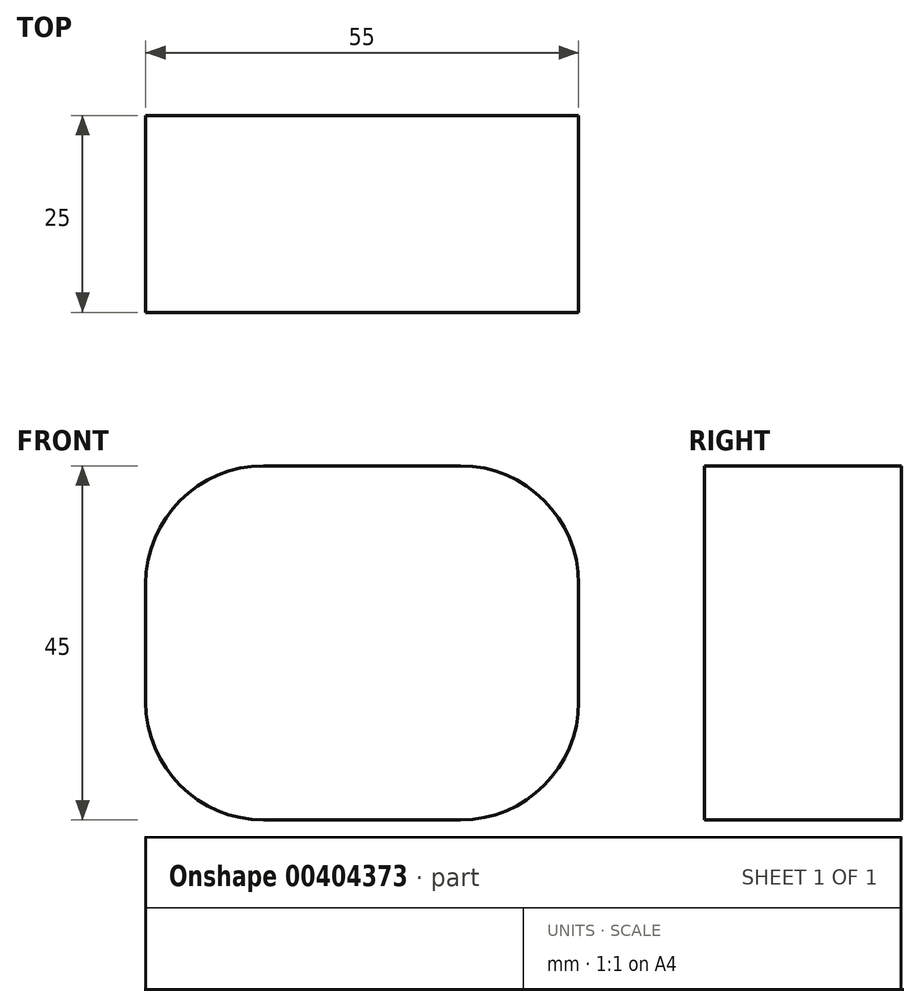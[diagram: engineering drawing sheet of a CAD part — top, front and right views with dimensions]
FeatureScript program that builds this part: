
annotation { "Feature Type Name" : "Feature", "Feature Type Description" : "" }
export const myFeature = defineFeature(function(context is Context, id is Id, definition is map)
    precondition{}
    {
        {
            var Q0;
            Q0=qCreatedBy(makeId("Front.planeOp"),FACE);
            var sketch = newSketch(context, id + "F0", { "sketchPlane" : qUnion([Q0])});
            skLineSegment(sketch, "E0.bottom", {"start": v(-12.5, 22.5) * mm, "end": v(12.5, 22.5) * mm});
            skLineSegment(sketch, "E0.top", {"start": v(-12.5, -22.5) * mm, "end": v(12.5, -22.5) * mm});
            skLineSegment(sketch, "E0.left", {"start": v(-27.5, 7.5) * mm, "end": v(-27.5, -7.5) * mm});
            skLineSegment(sketch, "E0.right", {"start": v(27.5, 7.5) * mm, "end": v(27.5, -7.5) * mm});
            skPoint(sketch, "E0.middle", {"position": v(0, 0) * mm});
            skPoint(sketch, "E1.visualSharp", {"position": v(-27.5, 22.5) * mm});
            skArc(sketch, "E1.filletArc", {"start": v(-12.5, 22.5) * mm, "mid": v(-23.1, 18.1) * mm, "end": v(-27.5, 7.5) * mm});
            skPoint(sketch, "E2.visualSharp", {"position": v(27.5, 22.5) * mm});
            skArc(sketch, "E2.filletArc", {"start": v(27.5, 7.5) * mm, "mid": v(23.1, 18.1) * mm, "end": v(12.5, 22.5) * mm});
            skPoint(sketch, "E3.visualSharp", {"position": v(27.5, -22.5) * mm});
            skArc(sketch, "E3.filletArc", {"start": v(12.5, -22.5) * mm, "mid": v(23.1, -18.1) * mm, "end": v(27.5, -7.5) * mm});
            skPoint(sketch, "E4.visualSharp", {"position": v(-27.5, -22.5) * mm});
            skArc(sketch, "E4.filletArc", {"start": v(-27.5, -7.5) * mm, "mid": v(-23.1, -18.1) * mm, "end": v(-12.5, -22.5) * mm});
            skSolve(sketch);
        }
        {
            var Q0;
            Q0=makeQuery(id+"F0.imprint","IMPRINT",FACE,{"disambiguationData":[TD([[makeQuery(id+"F0.imprint","IMPRINT",EDGE,{"derivedFrom":sQuery(id+"F0.wireOp",EDGE,"E0.bottom")}),-1.0]])]});
            extrude(context, id + "F1", {"entities" : qUnion([Q0]), "depth" : 25 * mm});
        }
    });
